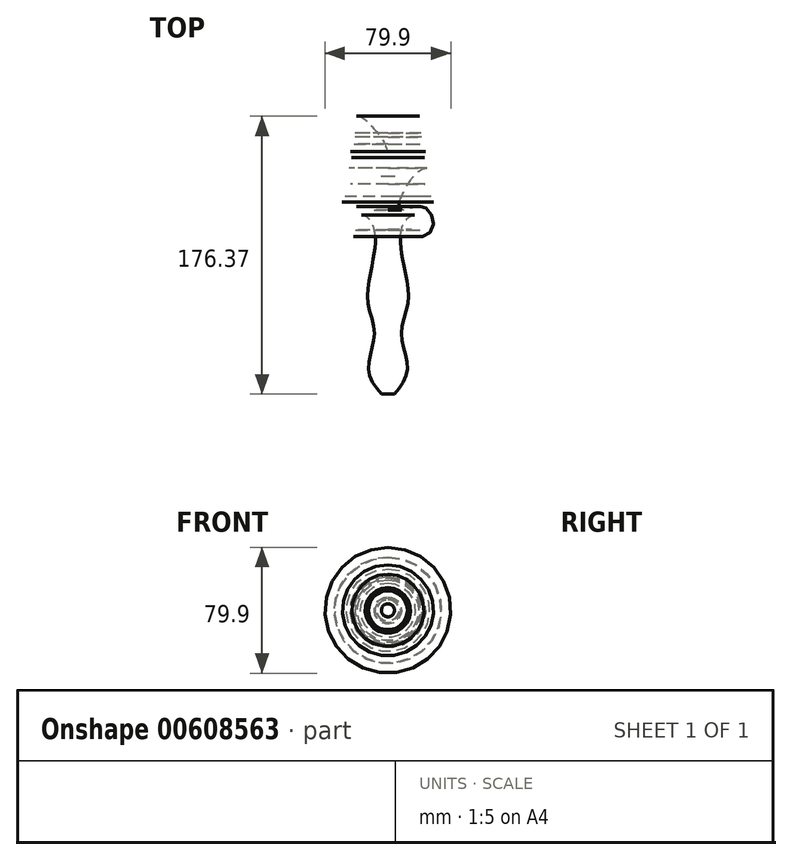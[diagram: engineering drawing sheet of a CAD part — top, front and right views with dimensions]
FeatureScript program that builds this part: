
annotation { "Feature Type Name" : "Feature", "Feature Type Description" : "" }
export const myFeature = defineFeature(function(context is Context, id is Id, definition is map)
    precondition{}
    {
        {
            var Q0;
            Q0=qCreatedBy(makeId("Right.planeOp"),FACE);
            var sketch = newSketch(context, id + "F0", { "sketchPlane" : qUnion([Q0])});
            skLineSegment(sketch, "E0", {"start": v(0, 0) * mm, "end": v(153.32, 0) * mm});
            skLineSegment(sketch, "E1", {"start": v(0, 4.2) * mm, "end": v(0, 0) * mm});
            skFitSpline(sketch, "E2", {"points": [v(0, 4.2) * mm, v(15.5, 12.33) * mm, v(38.18, 8.63) * mm, v(58.64, 12.82) * mm, v(84.04, 9.62) * mm, v(107.96, 9.86) * mm, v(113.13, 18.74) * mm, v(104.5, 22.2) * mm, v(104.75, 14.55) * mm, v(100.07, 21.2) * mm, v(107.7, 28.85) * mm, v(119.05, 21.45) * mm, v(117.08, 7.64) * mm, v(131.13, 11.59) * mm, v(143.46, 24.9) * mm, v(134.58, 34.03) * mm, v(125.7, 28.1) * mm, v(128.67, 23.67) * mm, v(133.35, 23.67) * mm, v(128.42, 20.46) * mm, v(122, 26.88) * mm, v(124.72, 36.24) * mm, v(134.1, 39.94) * mm, v(143.46, 35.75) * mm, v(149.13, 27.37) * mm, v(149.13, 19.23) * mm, v(138.53, 4.2) * mm, v(156.28, 10.36) * mm, v(165.65, 22.44) * mm, v(160.23, 25.89) * mm, v(159.49, 19.48) * mm, v(162.94, 21.45) * mm, v(161.21, 18.25) * mm, v(155.54, 18.5) * mm, v(154.06, 26.38) * mm, v(158, 32.3) * mm, v(169.84, 31.8) * mm, v(176.25, 18.5) * mm, v(169.84, 10.1) * mm, v(162.94, 4.2) * mm, v(153.32, 0) * mm], "startDerivative": vector(453.62, 367.32) * mm, "endDerivative": vector(-422.65, -149.13) * mm});
            skSolve(sketch);
        }
        {
            var Q0;
            Q0=makeQuery(id+"F0.imprint","IMPRINT",FACE,{"disambiguationData":[TD([[makeQuery(id+"F0.imprint","IMPRINT",EDGE,{"derivedFrom":sQuery(id+"F0.wireOp",EDGE,"E0")}),1.0]])]});
            var Q1;
            Q1=sQuery(id+"F0.wireOp",EDGE,"E0");
            revolve(context, id + "F1", {"entities" : qUnion([Q0]), "axis" : qUnion([Q1]), "revolveType" : RevolveType.FULL});
        }
    });
